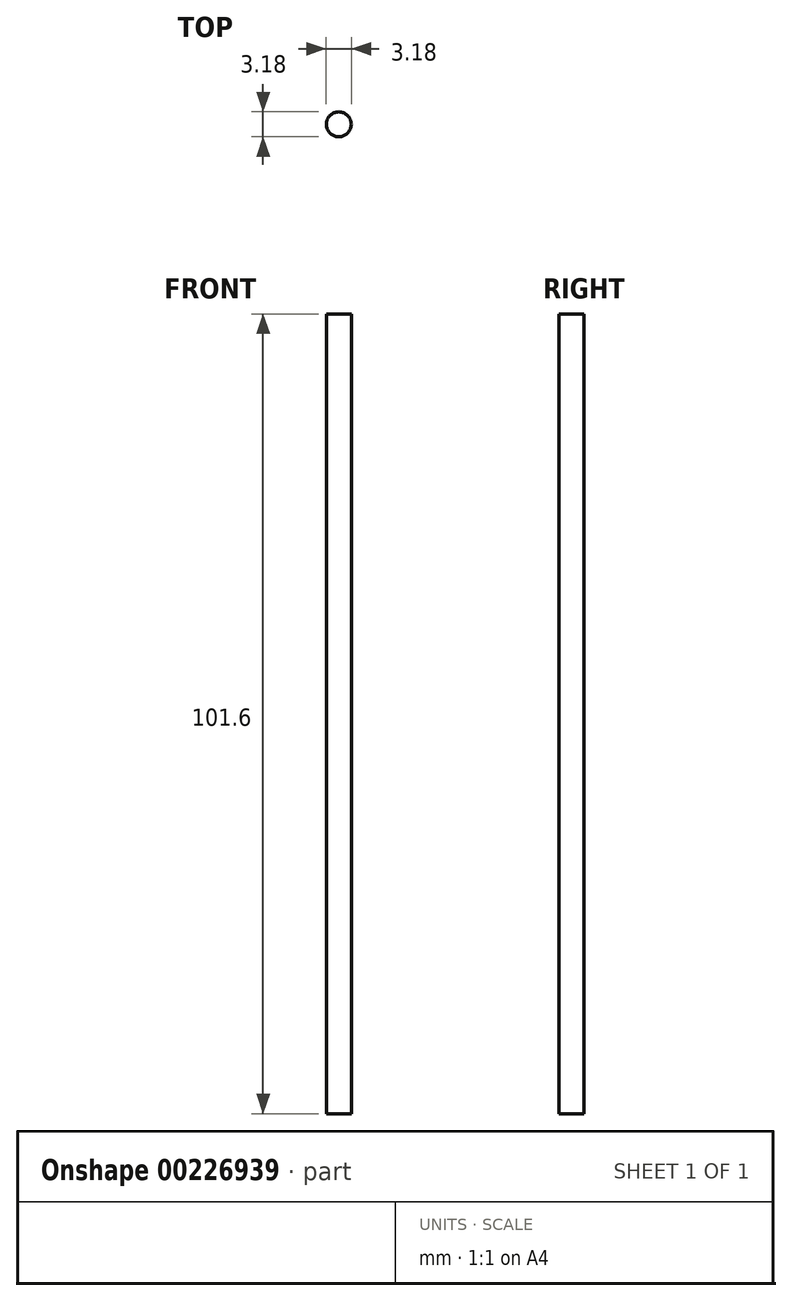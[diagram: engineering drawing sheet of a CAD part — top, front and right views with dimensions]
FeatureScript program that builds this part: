
annotation { "Feature Type Name" : "Feature", "Feature Type Description" : "" }
export const myFeature = defineFeature(function(context is Context, id is Id, definition is map)
    precondition{}
    {
        {
            var Q0;
            Q0=qCreatedBy(makeId("Top.planeOp"),FACE);
            var sketch = newSketch(context, id + "F0", { "sketchPlane" : qUnion([Q0])});
            skCircle(sketch, "E0", {"center": v(-25.63, 33.26) * mm, "radius": 1.59 * mm});
            skSolve(sketch);
        }
        {
            var Q0;
            Q0=makeQuery(id+"F0.imprint","IMPRINT",FACE,{"disambiguationData":[TD([[makeQuery(id+"F0.imprint","IMPRINT",EDGE,{"derivedFrom":sQuery(id+"F0.wireOp",EDGE,"E0")}),1.0]])]});
            extrude(context, id + "F1", {"entities" : qUnion([Q0]), "depth" : 101.6 * mm});
        }
    });
